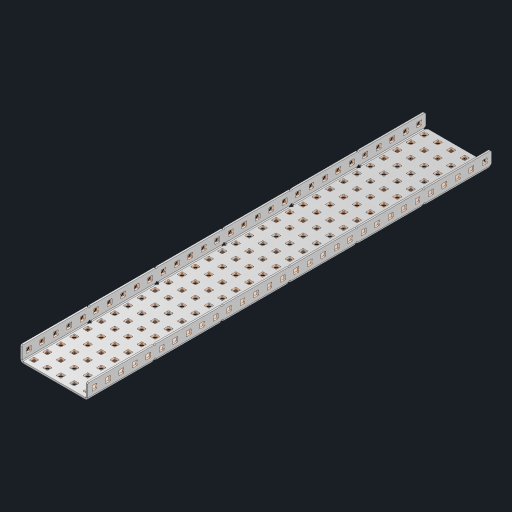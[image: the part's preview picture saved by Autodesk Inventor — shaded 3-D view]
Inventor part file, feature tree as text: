
AUTODESK INVENTOR PART (.ipt)
format: ipt  version: 2023 (Build 270158000, 158)  size: 2,279,424 bytes
history: native  units: in
note: dims shown in document units (in); Inventor stores cm internally (conversion verified against a paired STEP export)
features: other x215, extrude x209, sheet_metal_op x10, sketch x8, mirror x1, pattern_linear x1, chamfer x1
ambient origin geometry x8: Origin, YZ Plane, XZ Plane, XY Plane, X Axis, Y Axis, Z Axis, Center Point
bodies: Solid1 (feature_tree), Body (feature_tree)
feature tree (445):
  other  "Flange Pattern Plane"
  sheet_metal_op  "Flange Pattern"
  sheet_metal_op  "Body Pattern"
  other  "Arc Length"
  mirror  "Notch Mirror"
  pattern_linear  "Notch Pattern"  Spacing1=0.25in  [1 undecoded]
  chamfer  "End Chamfer"
  extrude  "Half Cut"  Depth=0.0625in
  sketch  "Sketch1"  dims[d0=2.5in]
  other  "Plate1"
  sketch  "Sketch2"  dims[d1=15.0in]
  other  "Plate2"
  sheet_metal_op  "Bend1"
  sheet_metal_op  "Corner1"
  sketch  "Sketch3"  dims[d2=0.0625in]
  other  "Flange Pattern Sketch"
  sketch  "Sketch7"  dims[d3=0.0625in]
  other  "Srf1"
  other  "Srf2"
  sketch  "Sketch8"  dims[d4=0.0312in]
  sketch  "Sketch9"  dims[d5=0.125in]
  other  "Srf91"
  sheet_metal_op  "Body Pattern Sketch"
  other  "Srf92"
  sketch  "Sketch13"  dims[d6=0.0625in]
  sketch  "Sketch14"  dims[d7=0.5in d8=90.0deg d9=0.0312in d10=0.25in d11=0.0625in d12=0.0625in d16=0.182in d17=0.02in d18=0.0625in d19=0.0in d20=0.25in d21=0.25in d46=0.172in d47=1.0in d48=0.0in d49=0.182in d50=0.02in d51=0.25in d52=0.25in d53=0.0625in d54=0.0in d55=0.172in d56=1.0in d57=0.0in d60=11.811in d62=0.5in d63=1.9685in d65=0.5in d85=0.1473in d86=0.1782in d88=0.04in d89=0.0625in d90=0.0in d91=0.04in d92=0.0491in d95=2.5in d96=0.04in d97=0.25in d98=45.0deg d101=0.0in d102=2.497in d131=2.5in d132=11.811in d134=0.5in d139=0.5in]
  other  "Srf856"
  other  "Srf1310"
  other  "Srf1311"
  other  "Srf1312"
  other  "Srf1376"
  other  "Srf1377"
  other  "Srf1728"
  other  "Srf1755"
  other  "Srf1878"
  other  "Srf1879"
  other  "Srf1880"
  other  "Srf1881"
  other  "Srf1882"
  other  "Srf1883"
  other  "Srf1884"
  other  "Srf1885"
  other  "Srf1886"
  other  "Srf1887"
  other  "Srf1888"
  other  "Srf1889"
  other  "Srf1890"
  other  "Srf1891"
  other  "Srf1892"
  other  "Srf1893"
  other  "Srf1894"
  other  "Srf1895"
  other  "Srf1896"
  other  "Srf1897"
  other  "Srf1898"
  other  "Srf1899"
  other  "Srf1900"
  other  "Srf1901"
  other  "Srf1902"
  other  "Srf1903"
  other  "Srf1904"
  other  "Srf1905"
  other  "Srf1906"
  other  "Srf1942"
  other  "Srf1943"
  other  "Srf1944"
  other  "Srf1945"
  other  "Srf1946"
  other  "Srf1947"
  other  "Srf1948"
  other  "Srf1949"
  other  "Srf1950"
  other  "Srf1951"
  other  "Srf1952"
  other  "Srf1953"
  other  "Srf1954"
  other  "Srf1955"
  other  "Srf1956"
  other  "Srf1957"
  other  "Srf1958"
  other  "Srf1959"
  other  "Srf1960"
  other  "Srf1961"
  other  "Srf1962"
  other  "Srf1963"
  other  "Srf1964"
  other  "Srf1965"
  other  "Srf1966"
  other  "Srf1967"
  other  "Srf1968"
  other  "Srf1969"
  other  "Srf1970"
  other  "Srf2111"
  other  "Srf2112"
  other  "Srf2113"
  other  "Srf2114"
  other  "Srf2115"
  other  "Srf2116"
  other  "Srf2117"
  other  "Srf2118"
  other  "Srf2119"
  other  "Srf2120"
  other  "Srf2121"
  other  "Srf2122"
  other  "Srf2123"
  other  "Srf2124"
  other  "Srf2125"
  other  "Srf2126"
  other  "Srf2127"
  other  "Srf2128"
  other  "Srf2129"
  other  "Srf2130"
  other  "Srf2131"
  other  "Srf2132"
  other  "Srf2133"
  other  "Srf2134"
  other  "Srf2135"
  other  "Srf2146"
  other  "Srf2147"
  other  "Srf2148"
  other  "Srf2149"
  other  "Srf2150"
  other  "Srf2151"
  other  "Srf2152"
  other  "Srf2153"
  other  "Srf2154"
  other  "Srf2155"
  other  "Srf2156"
  other  "Srf2157"
  other  "Srf2158"
  other  "Srf2159"
  other  "Srf2160"
  other  "Srf2161"
  other  "Srf2162"
  other  "Srf2163"
  other  "Srf2164"
  other  "Srf2165"
  other  "Srf2166"
  other  "Srf2167"
  other  "Srf2168"
  other  "Srf2169"
  other  "Srf2170"
  other  "Srf2171"
  other  "Srf2172"
  other  "Srf2173"
  other  "Srf2174"
  other  "Srf2175"
  other  "Srf2176"
  other  "Srf2177"
  other  "Srf2178"
  other  "Srf2179"
  other  "Srf2180"
  other  "Srf2181"
  other  "Srf2182"
  other  "Srf2183"
  other  "Srf2184"
  other  "Srf2185"
  other  "Srf2186"
  other  "Srf2187"
  other  "Srf2188"
  other  "Srf2189"
  other  "Srf2190"
  other  "Srf2191"
  other  "Srf2192"
  other  "Srf2193"
  other  "Srf2194"
  other  "Srf2195"
  other  "Srf2196"
  other  "Srf2197"
  other  "Srf2198"
  other  "Srf2199"
  other  "Srf2200"
  other  "Srf2201"
  other  "Srf2202"
  other  "Srf2203"
  other  "Srf2204"
  other  "Srf2205"
  other  "Srf2206"
  other  "Srf2207"
  other  "Srf2208"
  other  "Srf2209"
  other  "Srf2210"
  other  "Srf2211"
  other  "Srf2212"
  other  "Srf2213"
  other  "Srf2214"
  other  "Srf2215"
  other  "Srf2216"
  other  "Srf2217"
  other  "Srf2218"
  other  "Srf2219"
  other  "Srf2220"
  other  "Srf2221"
  other  "Srf2222"
  other  "Srf2223"
  other  "Srf2224"
  other  "Srf2225"
  other  "Srf2226"
  other  "Srf2227"
  other  "Srf2228"
  other  "Srf2229"
  other  "Srf2230"
  other  "Srf2231"
  other  "Srf2232"
  other  "Srf2233"
  other  "Srf2234"
  other  "Srf2235"
  other  "Srf2236"
  other  "Srf2237"
  other  "Srf2238"
  other  "Srf2239"
  other  "Srf2240"
  other  "Srf2241"
  other  "Srf2242"
  other  "Srf2243"
  other  "Srf2244"
  other  "Srf2245"
  other  "Srf2246"
  other  "Srf2247"
  other  "Srf2248"
  other  "Srf2249"
  other  "Srf2250"
  other  "Srf2251"
  other  "Srf2252"
  other  "Srf2253"
  other  "Srf2254"
  other  "Srf2255"
  other  "Srf2256"
  other  "Srf2257"
  other  "Srf2258"
  other  "Srf2259"
  other  "Srf2260"
  sheet_metal_op  "Flange Stamp"
  sheet_metal_op  "Flange Circle"
  sheet_metal_op  "Body Stamp"
  sheet_metal_op  "Body Circle"
  sheet_metal_op  "Notch"
  extrude  "ExtrusionSrf2"  Depth=0.0625in
  extrude  "ExtrusionSrf92"  Depth=2.5in
  extrude  "ExtrusionSrf856"  Depth=0.02in
  extrude  "ExtrusionSrf1310"  Depth=0.0625in
  extrude  "ExtrusionSrf1311"  TaperAngle=0.0deg  [1 undecoded]
  extrude  "ExtrusionSrf1312"  Depth=0.25in
  extrude  "ExtrusionSrf1376"  Depth=0.25in
  extrude  "ExtrusionSrf1377"  Depth=2.5in
  extrude  "ExtrusionSrf1728"  Depth=2.5in TaperAngle=0.0deg
  extrude  "ExtrusionSrf1755"  Depth=2.5in
  extrude  "ExtrusionSrf1878"  Depth=0.02in
  extrude  "ExtrusionSrf1879"  Depth=0.25in
  extrude  "ExtrusionSrf1880"  Depth=0.25in
  extrude  "ExtrusionSrf1881"  Depth=0.0625in
  extrude  "ExtrusionSrf1882"  TaperAngle=0.0deg  [1 undecoded]
  extrude  "ExtrusionSrf1883"  Depth=2.5in
  extrude  "ExtrusionSrf1884"  Depth=2.5in TaperAngle=0.0deg
  extrude  "ExtrusionSrf1885"  Depth=2.5in
  extrude  "ExtrusionSrf1886"  Depth=2.5in
  extrude  "ExtrusionSrf1887"  Depth=2.5in
  extrude  "ExtrusionSrf1888"  Depth=2.5in
  extrude  "ExtrusionSrf1889"  Depth=2.5in
  extrude  "ExtrusionSrf1890"  Depth=0.0625in
  extrude  "ExtrusionSrf1891"  TaperAngle=0.0deg  [1 undecoded]
  extrude  "ExtrusionSrf1892"  Depth=2.5in
  extrude  "ExtrusionSrf1893"  Depth=2.5in
  extrude  "ExtrusionSrf1894"  Depth=2.5in
  extrude  "ExtrusionSrf1895"  Depth=0.25in TaperAngle=45.0deg
  extrude  "ExtrusionSrf1896"  TaperAngle=0.0deg  [1 undecoded]
  extrude  "ExtrusionSrf1897"  Depth=2.5in
  extrude  "ExtrusionSrf1898"  Depth=2.5in
  extrude  "ExtrusionSrf1899"  Depth=2.5in
  extrude  "ExtrusionSrf1900"  Depth=2.5in
  extrude  "ExtrusionSrf1901"  Depth=2.5in
  extrude  "ExtrusionSrf1902"  [1 undecoded]
  extrude  "ExtrusionSrf1903"  [1 undecoded]
  extrude  "ExtrusionSrf1904"  [1 undecoded]
  extrude  "ExtrusionSrf1905"  [1 undecoded]
  extrude  "ExtrusionSrf1906"  [1 undecoded]
  extrude  "ExtrusionSrf1942"  [1 undecoded]
  extrude  "ExtrusionSrf1943"  [1 undecoded]
  extrude  "ExtrusionSrf1944"  [1 undecoded]
  extrude  "ExtrusionSrf1945"  [1 undecoded]
  extrude  "ExtrusionSrf1946"  [1 undecoded]
  extrude  "ExtrusionSrf1947"  [1 undecoded]
  extrude  "ExtrusionSrf1948"  [1 undecoded]
  extrude  "ExtrusionSrf1949"  [1 undecoded]
  extrude  "ExtrusionSrf1950"  [1 undecoded]
  extrude  "ExtrusionSrf1951"  [1 undecoded]
  extrude  "ExtrusionSrf1952"  [1 undecoded]
  extrude  "ExtrusionSrf1953"  [1 undecoded]
  extrude  "ExtrusionSrf1954"  [1 undecoded]
  extrude  "ExtrusionSrf1955"  [1 undecoded]
  extrude  "ExtrusionSrf1956"  [1 undecoded]
  extrude  "ExtrusionSrf1957"  [1 undecoded]
  extrude  "ExtrusionSrf1958"  [1 undecoded]
  extrude  "ExtrusionSrf1959"  [1 undecoded]
  extrude  "ExtrusionSrf1960"  [1 undecoded]
  extrude  "ExtrusionSrf1961"  [1 undecoded]
  extrude  "ExtrusionSrf1962"  [1 undecoded]
  extrude  "ExtrusionSrf1963"  [1 undecoded]
  extrude  "ExtrusionSrf1964"  [1 undecoded]
  extrude  "ExtrusionSrf1965"  [1 undecoded]
  extrude  "ExtrusionSrf1966"  [1 undecoded]
  extrude  "ExtrusionSrf1967"  [1 undecoded]
  extrude  "ExtrusionSrf1968"  [1 undecoded]
  extrude  "ExtrusionSrf1969"  [1 undecoded]
  extrude  "ExtrusionSrf1970"  [1 undecoded]
  extrude  "ExtrusionSrf2111"  [1 undecoded]
  extrude  "ExtrusionSrf2112"  [1 undecoded]
  extrude  "ExtrusionSrf2113"  [1 undecoded]
  extrude  "ExtrusionSrf2114"  [1 undecoded]
  extrude  "ExtrusionSrf2115"  [1 undecoded]
  extrude  "ExtrusionSrf2116"  [1 undecoded]
  extrude  "ExtrusionSrf2117"  [1 undecoded]
  extrude  "ExtrusionSrf2118"  [1 undecoded]
  extrude  "ExtrusionSrf2119"  [1 undecoded]
  extrude  "ExtrusionSrf2120"  [1 undecoded]
  extrude  "ExtrusionSrf2121"  [1 undecoded]
  extrude  "ExtrusionSrf2122"  [1 undecoded]
  extrude  "ExtrusionSrf2123"  [1 undecoded]
  extrude  "ExtrusionSrf2124"  [1 undecoded]
  extrude  "ExtrusionSrf2125"  [1 undecoded]
  extrude  "ExtrusionSrf2126"  [1 undecoded]
  extrude  "ExtrusionSrf2127"  [1 undecoded]
  extrude  "ExtrusionSrf2128"  [1 undecoded]
  extrude  "ExtrusionSrf2129"  [1 undecoded]
  extrude  "ExtrusionSrf2130"  [1 undecoded]
  extrude  "ExtrusionSrf2131"  [1 undecoded]
  extrude  "ExtrusionSrf2132"  [1 undecoded]
  extrude  "ExtrusionSrf2133"  [1 undecoded]
  extrude  "ExtrusionSrf2134"  [1 undecoded]
  extrude  "ExtrusionSrf2135"  [1 undecoded]
  extrude  "ExtrusionSrf2146"  [1 undecoded]
  extrude  "ExtrusionSrf2147"  [1 undecoded]
  extrude  "ExtrusionSrf2148"  [1 undecoded]
  extrude  "ExtrusionSrf2149"  [1 undecoded]
  extrude  "ExtrusionSrf2150"  [1 undecoded]
  extrude  "ExtrusionSrf2151"  [1 undecoded]
  extrude  "ExtrusionSrf2152"  [1 undecoded]
  extrude  "ExtrusionSrf2153"  [1 undecoded]
  extrude  "ExtrusionSrf2154"  [1 undecoded]
  extrude  "ExtrusionSrf2155"  [1 undecoded]
  extrude  "ExtrusionSrf2156"  [1 undecoded]
  extrude  "ExtrusionSrf2157"  [1 undecoded]
  extrude  "ExtrusionSrf2158"  [1 undecoded]
  extrude  "ExtrusionSrf2159"  [1 undecoded]
  extrude  "ExtrusionSrf2160"  [1 undecoded]
  extrude  "ExtrusionSrf2161"  [1 undecoded]
  extrude  "ExtrusionSrf2162"  [1 undecoded]
  extrude  "ExtrusionSrf2163"  [1 undecoded]
  extrude  "ExtrusionSrf2164"  [1 undecoded]
  extrude  "ExtrusionSrf2165"  [1 undecoded]
  extrude  "ExtrusionSrf2166"  [1 undecoded]
  extrude  "ExtrusionSrf2167"  [1 undecoded]
  extrude  "ExtrusionSrf2168"  [1 undecoded]
  extrude  "ExtrusionSrf2169"  [1 undecoded]
  extrude  "ExtrusionSrf2170"  [1 undecoded]
  extrude  "ExtrusionSrf2171"  [1 undecoded]
  extrude  "ExtrusionSrf2172"  [1 undecoded]
  extrude  "ExtrusionSrf2173"  [1 undecoded]
  extrude  "ExtrusionSrf2174"  [1 undecoded]
  extrude  "ExtrusionSrf2175"  [1 undecoded]
  extrude  "ExtrusionSrf2176"  [1 undecoded]
  extrude  "ExtrusionSrf2177"  [1 undecoded]
  extrude  "ExtrusionSrf2178"  [1 undecoded]
  extrude  "ExtrusionSrf2179"  [1 undecoded]
  extrude  "ExtrusionSrf2180"  [1 undecoded]
  extrude  "ExtrusionSrf2181"  [1 undecoded]
  extrude  "ExtrusionSrf2182"  [1 undecoded]
  extrude  "ExtrusionSrf2183"  [1 undecoded]
  extrude  "ExtrusionSrf2184"  [1 undecoded]
  extrude  "ExtrusionSrf2185"  [1 undecoded]
  extrude  "ExtrusionSrf2186"  [1 undecoded]
  extrude  "ExtrusionSrf2187"  [1 undecoded]
  extrude  "ExtrusionSrf2188"  [1 undecoded]
  extrude  "ExtrusionSrf2189"  [1 undecoded]
  extrude  "ExtrusionSrf2190"  [1 undecoded]
  extrude  "ExtrusionSrf2191"  [1 undecoded]
  extrude  "ExtrusionSrf2192"  [1 undecoded]
  extrude  "ExtrusionSrf2193"  [1 undecoded]
  extrude  "ExtrusionSrf2194"  [1 undecoded]
  extrude  "ExtrusionSrf2195"  [1 undecoded]
  extrude  "ExtrusionSrf2196"  [1 undecoded]
  extrude  "ExtrusionSrf2197"  [1 undecoded]
  extrude  "ExtrusionSrf2198"  [1 undecoded]
  extrude  "ExtrusionSrf2199"  [1 undecoded]
  extrude  "ExtrusionSrf2200"  [1 undecoded]
  extrude  "ExtrusionSrf2201"  [1 undecoded]
  extrude  "ExtrusionSrf2202"  [1 undecoded]
  extrude  "ExtrusionSrf2203"  [1 undecoded]
  extrude  "ExtrusionSrf2204"  [1 undecoded]
  extrude  "ExtrusionSrf2205"  [1 undecoded]
  extrude  "ExtrusionSrf2206"  [1 undecoded]
  extrude  "ExtrusionSrf2207"  [1 undecoded]
  extrude  "ExtrusionSrf2208"  [1 undecoded]
  extrude  "ExtrusionSrf2209"  [1 undecoded]
  extrude  "ExtrusionSrf2210"  [1 undecoded]
  extrude  "ExtrusionSrf2211"  [1 undecoded]
  extrude  "ExtrusionSrf2212"  [1 undecoded]
  extrude  "ExtrusionSrf2213"  [1 undecoded]
  extrude  "ExtrusionSrf2214"  [1 undecoded]
  extrude  "ExtrusionSrf2215"  [1 undecoded]
  extrude  "ExtrusionSrf2216"  [1 undecoded]
  extrude  "ExtrusionSrf2217"  [1 undecoded]
  extrude  "ExtrusionSrf2218"  [1 undecoded]
  extrude  "ExtrusionSrf2219"  [1 undecoded]
  extrude  "ExtrusionSrf2220"  [1 undecoded]
  extrude  "ExtrusionSrf2221"  [1 undecoded]
  extrude  "ExtrusionSrf2222"  [1 undecoded]
  extrude  "ExtrusionSrf2223"  [1 undecoded]
  extrude  "ExtrusionSrf2224"  [1 undecoded]
  extrude  "ExtrusionSrf2225"  [1 undecoded]
  extrude  "ExtrusionSrf2226"  [1 undecoded]
  extrude  "ExtrusionSrf2227"  [1 undecoded]
  extrude  "ExtrusionSrf2228"  [1 undecoded]
  extrude  "ExtrusionSrf2229"  [1 undecoded]
  extrude  "ExtrusionSrf2230"  [1 undecoded]
  extrude  "ExtrusionSrf2231"  [1 undecoded]
  extrude  "ExtrusionSrf2232"  [1 undecoded]
  extrude  "ExtrusionSrf2233"  [1 undecoded]
  extrude  "ExtrusionSrf2234"  [1 undecoded]
  extrude  "ExtrusionSrf2235"  [1 undecoded]
  extrude  "ExtrusionSrf2236"  [1 undecoded]
  extrude  "ExtrusionSrf2237"  [1 undecoded]
  extrude  "ExtrusionSrf2238"  [1 undecoded]
  extrude  "ExtrusionSrf2239"  [1 undecoded]
  extrude  "ExtrusionSrf2240"  [1 undecoded]
  extrude  "ExtrusionSrf2241"  [1 undecoded]
  extrude  "ExtrusionSrf2242"  [1 undecoded]
  extrude  "ExtrusionSrf2243"  [1 undecoded]
  extrude  "ExtrusionSrf2244"  [1 undecoded]
  extrude  "ExtrusionSrf2245"  [1 undecoded]
  extrude  "ExtrusionSrf2246"  [1 undecoded]
  extrude  "ExtrusionSrf2247"  [1 undecoded]
  extrude  "ExtrusionSrf2248"  [1 undecoded]
  extrude  "ExtrusionSrf2249"  [1 undecoded]
  extrude  "ExtrusionSrf2250"  [1 undecoded]
  extrude  "ExtrusionSrf2251"  [1 undecoded]
  extrude  "ExtrusionSrf2252"  [1 undecoded]
  extrude  "ExtrusionSrf2253"  [1 undecoded]
  extrude  "ExtrusionSrf2254"  [1 undecoded]
  extrude  "ExtrusionSrf2255"  [1 undecoded]
  extrude  "ExtrusionSrf2256"  [1 undecoded]
  extrude  "ExtrusionSrf2257"  [1 undecoded]
  extrude  "ExtrusionSrf2258"  [1 undecoded]
  extrude  "ExtrusionSrf2259"  [1 undecoded]
  extrude  "ExtrusionSrf2260"  [1 undecoded]
note: 179 required parameter values undecoded (feature->parameter linkage not recoverable at this tier; creation-order binding heuristic only, values carry confidence <= 0.55)
